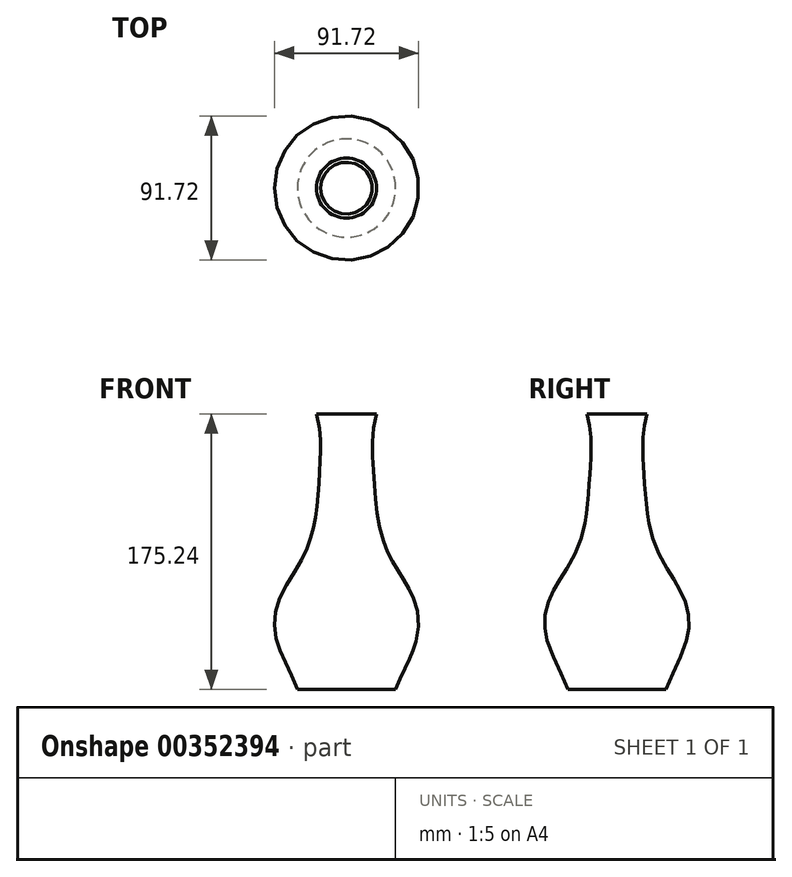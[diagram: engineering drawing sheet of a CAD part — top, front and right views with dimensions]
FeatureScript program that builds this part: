
annotation { "Feature Type Name" : "Feature", "Feature Type Description" : "" }
export const myFeature = defineFeature(function(context is Context, id is Id, definition is map)
    precondition{}
    {
        {
            var Q0;
            Q0=qCreatedBy(makeId("Front.planeOp"),FACE);
            var sketch = newSketch(context, id + "F0", { "sketchPlane" : qUnion([Q0])});
            skLineSegment(sketch, "E0", {"start": v(0, -38.87) * mm, "end": v(31.22, -38.87) * mm});
            skFitSpline(sketch, "E1", {"points": [v(31.22, -38.87) * mm, v(42.96, -11.99) * mm, v(44.6, 13.35) * mm, v(29.81, 41.46) * mm, v(21.82, 60.6) * mm, v(18.9, 77.04) * mm, v(17.26, 96.76) * mm, v(16.43, 113.6) * mm, v(19.05, 136.37) * mm], "startDerivative": vector(85.99, 231.27) * mm, "endDerivative": vector(62.46, 239.5) * mm});
            skLineSegment(sketch, "E2", {"start": v(19.05, 136.37) * mm, "end": v(0, 136.37) * mm});
            skLineSegment(sketch, "E3", {"start": v(0, 136.37) * mm, "end": v(0, -38.87) * mm});
            skSolve(sketch);
        }
        {
            var Q0;
            Q0=sQuery(id+"F0.wireOp",EDGE,"E1");
            var Q1;
            Q1=sQuery(id+"F0.wireOp",EDGE,"E0");
            var Q2;
            Q2=sQuery(id+"F0.wireOp",EDGE,"E3");
            revolve(context, id + "F1", {"bodyType" : ToolBodyType.SURFACE, "surfaceEntities" : qUnion([Q0, Q1]), "axis" : qUnion([Q2]), "revolveType" : RevolveType.FULL});
        }
    });
